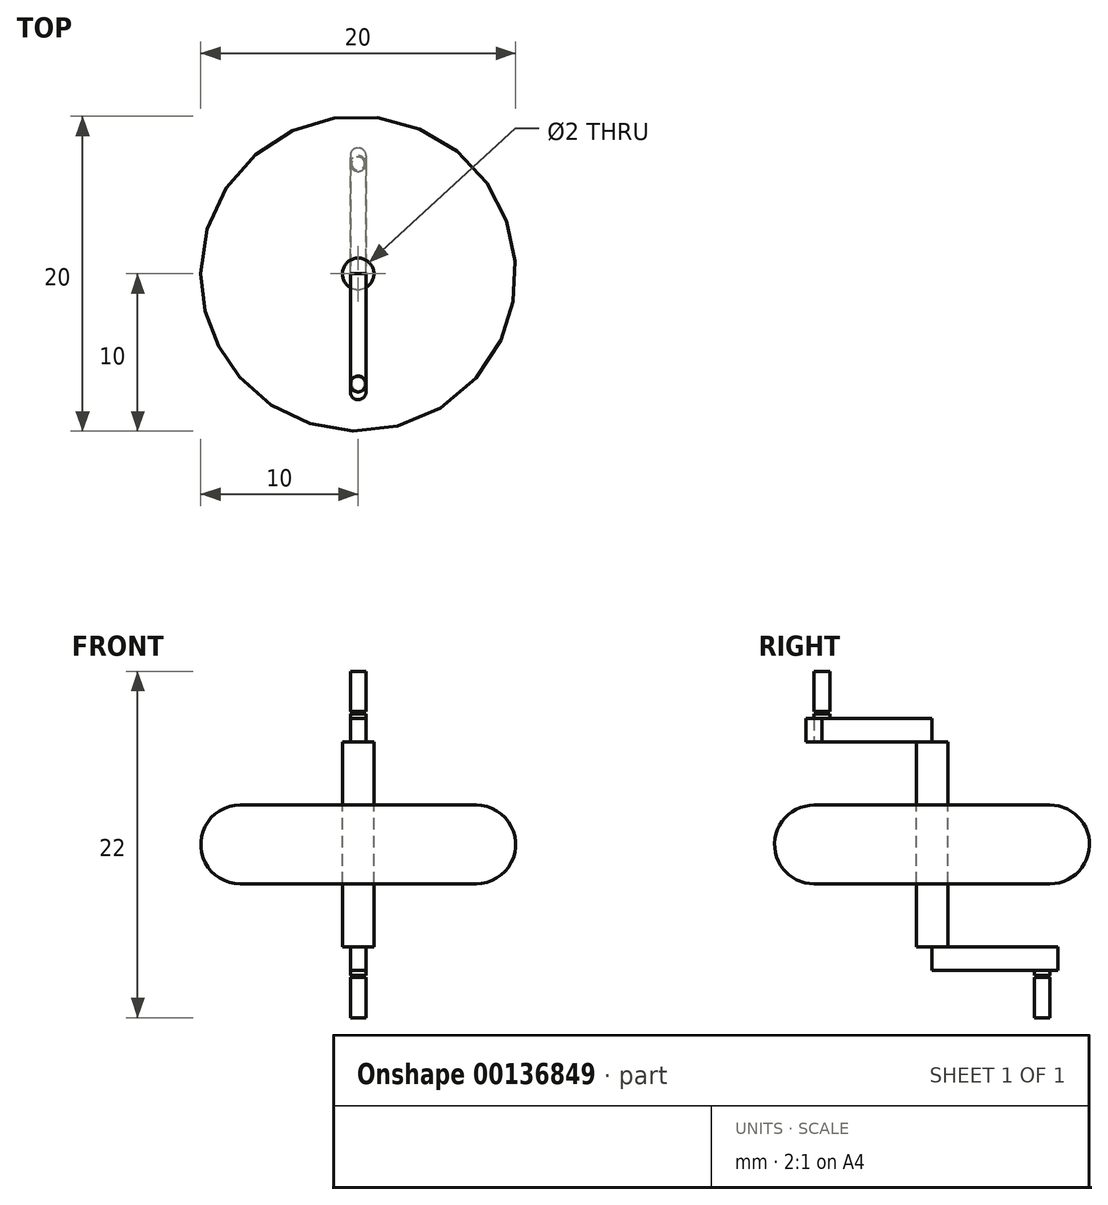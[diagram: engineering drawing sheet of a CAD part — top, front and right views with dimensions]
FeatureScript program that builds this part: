
annotation { "Feature Type Name" : "Feature", "Feature Type Description" : "" }
export const myFeature = defineFeature(function(context is Context, id is Id, definition is map)
    precondition{}
    {
        {
            var Q0;
            Q0=qCreatedBy(makeId("Front.planeOp"),FACE);
            var sketch = newSketch(context, id + "F0", { "sketchPlane" : qUnion([Q0])});
            skLineSegment(sketch, "E0.bottom", {"start": v(1, -2.5) * mm, "end": v(-1, -2.5) * mm});
            skLineSegment(sketch, "E0.top", {"start": v(1, 2.5) * mm, "end": v(-1, 2.5) * mm});
            skLineSegment(sketch, "E0.left", {"start": v(1, -2.5) * mm, "end": v(1, 2.5) * mm});
            skLineSegment(sketch, "E0.right", {"start": v(-1, -2.5) * mm, "end": v(-1, 2.5) * mm});
            skPoint(sketch, "E0.middle", {"position": v(0, 0) * mm});
            skLineSegment(sketch, "E1", {"start": v(0, 2.5) * mm, "end": v(0, -2.5) * mm});
            skLineSegment(sketch, "E2.bottom", {"start": v(10, -2.5) * mm, "end": v(-10, -2.5) * mm});
            skLineSegment(sketch, "E2.top", {"start": v(10, 2.5) * mm, "end": v(-10, 2.5) * mm});
            skLineSegment(sketch, "E2.left", {"start": v(10, -2.5) * mm, "end": v(10, 2.5) * mm});
            skLineSegment(sketch, "E2.right", {"start": v(-10, -2.5) * mm, "end": v(-10, 2.5) * mm});
            skSolve(sketch);
        }
        {
            var Q0;
            {var subQ0=sQuery(id+"F0.wireOp",EDGE,"E0.left");Q0=makeQuery(id+"F0.imprint","IMPRINT",FACE,{"disambiguationData":[TD([[makeQuery(id+"F0.imprint","IMPRINT",EDGE,{"derivedFrom":subQ0}),-1.0]])]});}
            var Q1;
            Q1=sQuery(id+"F0.wireOp",EDGE,"E1");
            revolve(context, id + "F1", {"entities" : qUnion([Q0]), "axis" : qUnion([Q1]), "revolveType" : RevolveType.FULL});
        }
        {
            var Q0;
            Q0=makeQuery(id+"F1.opRevolve","SWEPT_EDGE",EDGE,{"disambiguationData":[OSD([sQuery(id+"F0.wireOp",EDGE,"E2.bottom"),sQuery(id+"F0.wireOp",EDGE,"E2.left")])]});
            var Q1;
            Q1=makeQuery(id+"F1.opRevolve","SWEPT_EDGE",EDGE,{"disambiguationData":[OSD([sQuery(id+"F0.wireOp",EDGE,"E2.top"),sQuery(id+"F0.wireOp",EDGE,"E2.left")])]});
            fillet(context, id + "F2", {"entities" : qUnion([Q0, Q1]), "radius" : 2.5 * mm, "tangentPropagation" : true, "allowEdgeOverflow" : false});
        }
        {
            var Q0;
            Q0=qCreatedBy(makeId("Right.planeOp"),FACE);
            var sketch = newSketch(context, id + "F3", { "sketchPlane" : qUnion([Q0])});
            skLineSegment(sketch, "E3.bottom", {"start": v(1, -8) * mm, "end": v(-1, -8) * mm});
            skLineSegment(sketch, "E3.top", {"start": v(1, 8) * mm, "end": v(-1, 8) * mm});
            skLineSegment(sketch, "E3.left", {"start": v(1, -8) * mm, "end": v(1, 8) * mm});
            skLineSegment(sketch, "E3.right", {"start": v(-1, -8) * mm, "end": v(-1, 8) * mm});
            skPoint(sketch, "E3.middle", {"position": v(0, 0) * mm});
            skLineSegment(sketch, "E4", {"start": v(0, 8) * mm, "end": v(0, -8) * mm});
            skLineSegment(sketch, "E5.bottom", {"start": v(1, 8) * mm, "end": v(-8, 8) * mm});
            skLineSegment(sketch, "E5.top", {"start": v(1, 6.5) * mm, "end": v(-8, 6.5) * mm});
            skLineSegment(sketch, "E5.left", {"start": v(1, 8) * mm, "end": v(1, 6.5) * mm});
            skLineSegment(sketch, "E5.right", {"start": v(-8, 8) * mm, "end": v(-8, 6.5) * mm});
            skLineSegment(sketch, "E6.bottom", {"start": v(-1, -8) * mm, "end": v(8, -8) * mm});
            skLineSegment(sketch, "E6.top", {"start": v(-1, -6.5) * mm, "end": v(8, -6.5) * mm});
            skLineSegment(sketch, "E6.left", {"start": v(-1, -8) * mm, "end": v(-1, -6.5) * mm});
            skLineSegment(sketch, "E6.right", {"start": v(8, -8) * mm, "end": v(8, -6.5) * mm});
            skLineSegment(sketch, "E7", {"start": v(7, -6.5) * mm, "end": v(7, -8) * mm});
            skLineSegment(sketch, "E8", {"start": v(-7, 8) * mm, "end": v(-7, 6.5) * mm});
            skLineSegment(sketch, "E9", {"start": v(-7.5, 8) * mm, "end": v(-7.5, 6.5) * mm});
            skLineSegment(sketch, "E10", {"start": v(-6.5, 8) * mm, "end": v(-6.5, 6.5) * mm});
            skLineSegment(sketch, "E11", {"start": v(7.5, -6.5) * mm, "end": v(7.5, -8) * mm});
            skLineSegment(sketch, "E12", {"start": v(6.5, -6.5) * mm, "end": v(6.5, -8) * mm});
            skSolve(sketch);
        }
        {
            var Q0;
            {var subQ3=sQuery(id+"F3.wireOp",EDGE,"E5.top");var subQ5=sQuery(id+"F3.wireOp",EDGE,"E4");var subQ6=makeQuery(id+"F3.imprint","INTERSECT",VERTEX,{"derivedFrom":[subQ5,subQ3]});Q0=makeQuery(id+"F3.imprint","IMPRINT",FACE,{"disambiguationData":[TD([[makeQuery(id+"F3.imprint","IMPRINT",EDGE,{"disambiguationData":[TD([[subQ6,-1.0]])],"derivedFrom":subQ5}),-1.0]])]});}
            var Q1;
            Q1=sQuery(id+"F3.wireOp",EDGE,"E4");
            revolve(context, id + "F4", {"entities" : qUnion([Q0]), "axis" : qUnion([Q1]), "revolveType" : RevolveType.FULL});
        }
        {
            var Q0;
            {var subQ0=sQuery(id+"F3.wireOp",EDGE,"E8");Q0=makeQuery(id+"F3.imprint","IMPRINT",FACE,{"disambiguationData":[TD([[makeQuery(id+"F3.imprint","IMPRINT",EDGE,{"derivedFrom":subQ0}),-1.0]])]});}
            var Q1;
            Q1=sQuery(id+"F3.wireOp",EDGE,"E9");
            var Q2;
            Q2=sQuery(id+"F3.wireOp",EDGE,"E8");
            revolve(context, id + "F5", {"bodyType" : ToolBodyType.SURFACE, "entities" : qUnion([Q0]), "surfaceEntities" : qUnion([Q1]), "axis" : qUnion([Q2]), "revolveType" : RevolveType.FULL});
        }
        {
            var Q0;
            Q0=sQuery(id+"F3.wireOp",EDGE,"E11");
            var Q1;
            Q1=sQuery(id+"F3.wireOp",EDGE,"E7");
            revolve(context, id + "F6", {"bodyType" : ToolBodyType.SURFACE, "surfaceEntities" : qUnion([Q0]), "axis" : qUnion([Q1]), "revolveType" : RevolveType.FULL});
        }
        {
            var Q0;
            {var subQ5=sQuery(id+"F3.wireOp",EDGE,"E10");Q0=makeQuery(id+"F3.imprint","IMPRINT",FACE,{"disambiguationData":[TD([[makeQuery(id+"F3.imprint","IMPRINT",EDGE,{"derivedFrom":subQ5}),1.0]])]});}
            var Q1;
            {var subQ0=sQuery(id+"F3.wireOp",EDGE,"E5.bottom");var subQ1=sQuery(id+"F3.wireOp",EDGE,"E3.right");var subQ2=makeQuery(id+"F3.imprint","INTERSECT",VERTEX,{"derivedFrom":[subQ1,subQ0]});Q1=makeQuery(id+"F3.imprint","IMPRINT",FACE,{"disambiguationData":[TD([[makeQuery(id+"F3.imprint","IMPRINT",EDGE,{"disambiguationData":[TD([[subQ2,1.0]])],"derivedFrom":subQ1}),-1.0]])]});}
            var Q2;
            {var subQ5=sQuery(id+"F3.wireOp",EDGE,"E5.left");Q2=makeQuery(id+"F3.imprint","IMPRINT",FACE,{"disambiguationData":[TD([[makeQuery(id+"F3.imprint","IMPRINT",EDGE,{"derivedFrom":subQ5}),-1.0]])]});}
            var Q3;
            {var subQ0=sQuery(id+"F3.wireOp",EDGE,"E5.right");Q3=makeQuery(id+"F3.imprint","IMPRINT",FACE,{"disambiguationData":[TD([[makeQuery(id+"F3.imprint","IMPRINT",EDGE,{"derivedFrom":subQ0}),1.0]])]});}
            var Q4;
            {var subQ0=sQuery(id+"F3.wireOp",EDGE,"E8");Q4=makeQuery(id+"F3.imprint","IMPRINT",FACE,{"disambiguationData":[TD([[makeQuery(id+"F3.imprint","IMPRINT",EDGE,{"derivedFrom":subQ0}),-1.0]])]});}
            var Q5;
            {var subQ0=sQuery(id+"F3.wireOp",EDGE,"E8");Q5=makeQuery(id+"F3.imprint","IMPRINT",FACE,{"disambiguationData":[TD([[makeQuery(id+"F3.imprint","IMPRINT",EDGE,{"derivedFrom":subQ0}),1.0]])]});}
            extrude(context, id + "F7", {"entities" : qUnion([Q0, Q1, Q2, Q3, Q4, Q5]), "operationType" : NewBodyOperationType.ADD, "depth" : 1 * mm, "symmetric" : true});
        }
        {
            var Q0;
            {var subQ5=sQuery(id+"F3.wireOp",EDGE,"E6.left");Q0=makeQuery(id+"F3.imprint","IMPRINT",FACE,{"disambiguationData":[TD([[makeQuery(id+"F3.imprint","IMPRINT",EDGE,{"derivedFrom":subQ5}),-1.0]])]});}
            var Q1;
            {var subQ0=sQuery(id+"F3.wireOp",EDGE,"E6.bottom");var subQ1=sQuery(id+"F3.wireOp",EDGE,"E3.left");var subQ2=makeQuery(id+"F3.imprint","INTERSECT",VERTEX,{"derivedFrom":[subQ1,subQ0]});Q1=makeQuery(id+"F3.imprint","IMPRINT",FACE,{"disambiguationData":[TD([[makeQuery(id+"F3.imprint","IMPRINT",EDGE,{"disambiguationData":[TD([[subQ2,-1.0]])],"derivedFrom":subQ1}),1.0]])]});}
            var Q2;
            {var subQ5=sQuery(id+"F3.wireOp",EDGE,"E12");Q2=makeQuery(id+"F3.imprint","IMPRINT",FACE,{"disambiguationData":[TD([[makeQuery(id+"F3.imprint","IMPRINT",EDGE,{"derivedFrom":subQ5}),-1.0]])]});}
            var Q3;
            {var subQ0=sQuery(id+"F3.wireOp",EDGE,"E7");Q3=makeQuery(id+"F3.imprint","IMPRINT",FACE,{"disambiguationData":[TD([[makeQuery(id+"F3.imprint","IMPRINT",EDGE,{"derivedFrom":subQ0}),-1.0]])]});}
            var Q4;
            {var subQ0=sQuery(id+"F3.wireOp",EDGE,"E7");Q4=makeQuery(id+"F3.imprint","IMPRINT",FACE,{"disambiguationData":[TD([[makeQuery(id+"F3.imprint","IMPRINT",EDGE,{"derivedFrom":subQ0}),1.0]])]});}
            var Q5;
            {var subQ0=sQuery(id+"F3.wireOp",EDGE,"E6.right");Q5=makeQuery(id+"F3.imprint","IMPRINT",FACE,{"disambiguationData":[TD([[makeQuery(id+"F3.imprint","IMPRINT",EDGE,{"derivedFrom":subQ0}),1.0]])]});}
            extrude(context, id + "F8", {"entities" : qUnion([Q0, Q1, Q2, Q3, Q4, Q5]), "operationType" : NewBodyOperationType.ADD, "depth" : 1 * mm, "symmetric" : true});
        }
        {
            var Q0;
            Q0=makeQuery(id+"F7.opExtrude","CAP_EDGE",EDGE,{"disambiguationData":[OSD([sQuery(id+"F3.wireOp",EDGE,"E5.right")])],"isStart":false});
            var Q1;
            Q1=makeQuery(id+"F7.opExtrude","CAP_EDGE",EDGE,{"disambiguationData":[OSD([sQuery(id+"F3.wireOp",EDGE,"E5.right")])],"isStart":true});
            var Q2;
            Q2=makeQuery(id+"F8.opExtrude","CAP_EDGE",EDGE,{"disambiguationData":[OSD([sQuery(id+"F3.wireOp",EDGE,"E6.right")])],"isStart":true});
            fillet(context, id + "F9", {"entities" : qUnion([Q0, Q1, Q2]), "radius" : 0.5 * mm, "tangentPropagation" : true, "allowEdgeOverflow" : false});
        }
        {
            var Q0;
            Q0=makeQuery(id+"F8.opExtrude","CAP_EDGE",EDGE,{"disambiguationData":[OSD([sQuery(id+"F3.wireOp",EDGE,"E6.right")])],"isStart":false});
            fillet(context, id + "F10", {"entities" : qUnion([Q0]), "radius" : 0.5 * mm, "tangentPropagation" : true, "allowEdgeOverflow" : false});
        }
        {
            var Q0;
            Q0=makeQuery(id+"F1.opRevolve","SWEPT_FACE",FACE,{"disambiguationData":[OSD([sQuery(id+"F0.wireOp",EDGE,"E2.top")])]});
            var sketch = newSketch(context, id + "F11", { "sketchPlane" : qUnion([Q0])});
            skCircle(sketch, "E13", {"center": v(0, -7) * mm, "radius": 0.5 * mm});
            skPoint(sketch, "E14", {"position": v(0, 7) * mm});
            skCircle(sketch, "E15", {"center": v(0, 7) * mm, "radius": 0.5 * mm});
            skSolve(sketch);
        }
        {
            var Q0;
            {var subQ0=sQuery(id+"F11.wireOp",EDGE,"E13");var subQ1=sQuery(id+"F0.wireOp",EDGE,"E2.top");var subQ2=makeQuery(id+"F2.opFillet","BLEND_EDGE",EDGE,{"blendedFrom":[makeQuery(id+"F1.opRevolve","SWEPT_EDGE",EDGE,{"disambiguationData":[OSD([subQ1,sQuery(id+"F0.wireOp",EDGE,"E2.left")])]}),makeQuery(id+"F1.opRevolve","SWEPT_FACE",FACE,{"disambiguationData":[OSD([subQ1])]})],"blendedInto":[makeQuery(id+"F1.opRevolve","SWEPT_FACE",FACE,{"disambiguationData":[OSD([subQ1])]})]});var subQ3=makeQuery(id+"F11.imprint","INTERSECT",VERTEX,{"disambiguationData":[OD(0.0)],"derivedFrom":[subQ2,subQ0]});Q0=makeQuery(id+"F11.imprint","IMPRINT",FACE,{"disambiguationData":[TD([[makeQuery(id+"F11.imprint","IMPRINT",EDGE,{"disambiguationData":[TD([[subQ3,1.0]])],"derivedFrom":subQ0}),1.0]])]});}
            extrude(context, id + "F12", {"entities" : qUnion([Q0]), "operationType" : NewBodyOperationType.REMOVE, "depth" : 10 * mm});
        }
        {
            var Q0;
            Q0=qCreatedBy(makeId("Right.planeOp"),FACE);
            var sketch = newSketch(context, id + "F13", { "sketchPlane" : qUnion([Q0])});
            skLineSegment(sketch, "E16.bottom", {"start": v(7.5, -6.5) * mm, "end": v(6.5, -6.5) * mm});
            skLineSegment(sketch, "E16.top", {"start": v(7.5, -11) * mm, "end": v(6.5, -11) * mm});
            skLineSegment(sketch, "E16.left", {"start": v(7.5, -6.5) * mm, "end": v(7.5, -8.3) * mm});
            skLineSegment(sketch, "E16.right", {"start": v(6.5, -6.5) * mm, "end": v(6.5, -8.3) * mm});
            skLineSegment(sketch, "E17", {"start": v(7, -6.5) * mm, "end": v(7, -11) * mm});
            skLineSegment(sketch, "E18.bottom", {"start": v(-7.5, 6.5) * mm, "end": v(-6.5, 6.5) * mm});
            skLineSegment(sketch, "E18.top", {"start": v(-7.5, 11) * mm, "end": v(-6.5, 11) * mm});
            skLineSegment(sketch, "E18.left", {"start": v(-7.5, 6.5) * mm, "end": v(-7.5, 8.3) * mm});
            skLineSegment(sketch, "E18.right", {"start": v(-6.5, 6.5) * mm, "end": v(-6.5, 8.3) * mm});
            skLineSegment(sketch, "E19", {"start": v(-7, 6.5) * mm, "end": v(-7, 11) * mm});
            skLineSegment(sketch, "E20.bottom", {"start": v(7.5, -8.3) * mm, "end": v(6.5, -8.3) * mm});
            skLineSegment(sketch, "E20.top", {"start": v(7.5, -8.45) * mm, "end": v(6.5, -8.45) * mm});
            skLineSegment(sketch, "E21.bottom", {"start": v(-7.5, 8.45) * mm, "end": v(-6.5, 8.45) * mm});
            skLineSegment(sketch, "E21.top", {"start": v(-7.5, 8.3) * mm, "end": v(-6.5, 8.3) * mm});
            skLineSegment(sketch, "E22", {"start": v(-6.58, 8.45) * mm, "end": v(-6.58, 8.3) * mm});
            skLineSegment(sketch, "E23", {"start": v(-7.42, 8.45) * mm, "end": v(-7.42, 8.3) * mm});
            skLineSegment(sketch, "E24.trimOffspring", {"start": v(-6.5, 8.45) * mm, "end": v(-6.5, 11) * mm});
            skLineSegment(sketch, "E25.trimOffspring", {"start": v(-7.5, 8.45) * mm, "end": v(-7.5, 11) * mm});
            skLineSegment(sketch, "E26", {"start": v(7.42, -8.3) * mm, "end": v(7.42, -8.45) * mm});
            skLineSegment(sketch, "E27", {"start": v(6.58, -8.3) * mm, "end": v(6.58, -8.45) * mm});
            skLineSegment(sketch, "E28.trimOffspring", {"start": v(6.5, -8.45) * mm, "end": v(6.5, -11) * mm});
            skLineSegment(sketch, "E29.trimOffspring", {"start": v(7.5, -8.45) * mm, "end": v(7.5, -11) * mm});
            skSolve(sketch);
        }
        {
            var Q0;
            {var subQ0=sQuery(id+"F13.wireOp",EDGE,"E16.left");Q0=makeQuery(id+"F13.imprint","IMPRINT",FACE,{"disambiguationData":[TD([[makeQuery(id+"F13.imprint","IMPRINT",EDGE,{"derivedFrom":subQ0}),-1.0]])]});}
            var Q1;
            Q1=sQuery(id+"F13.wireOp",EDGE,"E17");
            revolve(context, id + "F14", {"operationType" : NewBodyOperationType.ADD, "entities" : qUnion([Q0]), "axis" : qUnion([Q1]), "revolveType" : RevolveType.FULL});
        }
        {
            var Q0;
            {var subQ0=sQuery(id+"F13.wireOp",EDGE,"E18.right");Q0=makeQuery(id+"F13.imprint","IMPRINT",FACE,{"disambiguationData":[TD([[makeQuery(id+"F13.imprint","IMPRINT",EDGE,{"derivedFrom":subQ0}),1.0]])]});}
            var Q1;
            Q1=sQuery(id+"F13.wireOp",EDGE,"E19");
            revolve(context, id + "F15", {"operationType" : NewBodyOperationType.ADD, "entities" : qUnion([Q0]), "axis" : qUnion([Q1]), "revolveType" : RevolveType.FULL});
        }
        {
            var Q0;
            {var subQ0=sQuery(id+"F13.wireOp",EDGE,"E29.trimOffspring");Q0=makeQuery(id+"F13.imprint","IMPRINT",FACE,{"disambiguationData":[TD([[makeQuery(id+"F13.imprint","IMPRINT",EDGE,{"derivedFrom":subQ0}),-1.0]])]});}
            var Q1;
            {var subQ5=sQuery(id+"F13.wireOp",EDGE,"E26");Q1=makeQuery(id+"F13.imprint","IMPRINT",FACE,{"disambiguationData":[TD([[makeQuery(id+"F13.imprint","IMPRINT",EDGE,{"derivedFrom":subQ5}),-1.0]])]});}
            var Q2;
            Q2=sQuery(id+"F13.wireOp",EDGE,"E17");
            revolve(context, id + "F16", {"operationType" : NewBodyOperationType.ADD, "entities" : qUnion([Q0, Q1]), "axis" : qUnion([Q2]), "revolveType" : RevolveType.FULL});
        }
        {
            var Q0;
            {var subQ0=sQuery(id+"F13.wireOp",EDGE,"E24.trimOffspring");Q0=makeQuery(id+"F13.imprint","IMPRINT",FACE,{"disambiguationData":[TD([[makeQuery(id+"F13.imprint","IMPRINT",EDGE,{"derivedFrom":subQ0}),1.0]])]});}
            var Q1;
            {var subQ5=sQuery(id+"F13.wireOp",EDGE,"E22");Q1=makeQuery(id+"F13.imprint","IMPRINT",FACE,{"disambiguationData":[TD([[makeQuery(id+"F13.imprint","IMPRINT",EDGE,{"derivedFrom":subQ5}),-1.0]])]});}
            var Q2;
            Q2=sQuery(id+"F13.wireOp",EDGE,"E19");
            revolve(context, id + "F17", {"operationType" : NewBodyOperationType.ADD, "entities" : qUnion([Q0, Q1]), "axis" : qUnion([Q2]), "revolveType" : RevolveType.FULL});
        }
        {
            var Q0;
            Q0=makeQuery(id+"F5.opRevolve","SWEPT_BODY",BODY,{"disambiguationData":[OSD([sQuery(id+"F3.wireOp",EDGE,"E9")])]});
            var Q1;
            Q1=makeQuery(id+"F6.opRevolve","SWEPT_BODY",BODY,{"disambiguationData":[OSD([sQuery(id+"F3.wireOp",EDGE,"E11")])]});
            deleteBodies(context, id + "F18", {"entities" : qUnion([Q0, Q1])});
        }
    });
